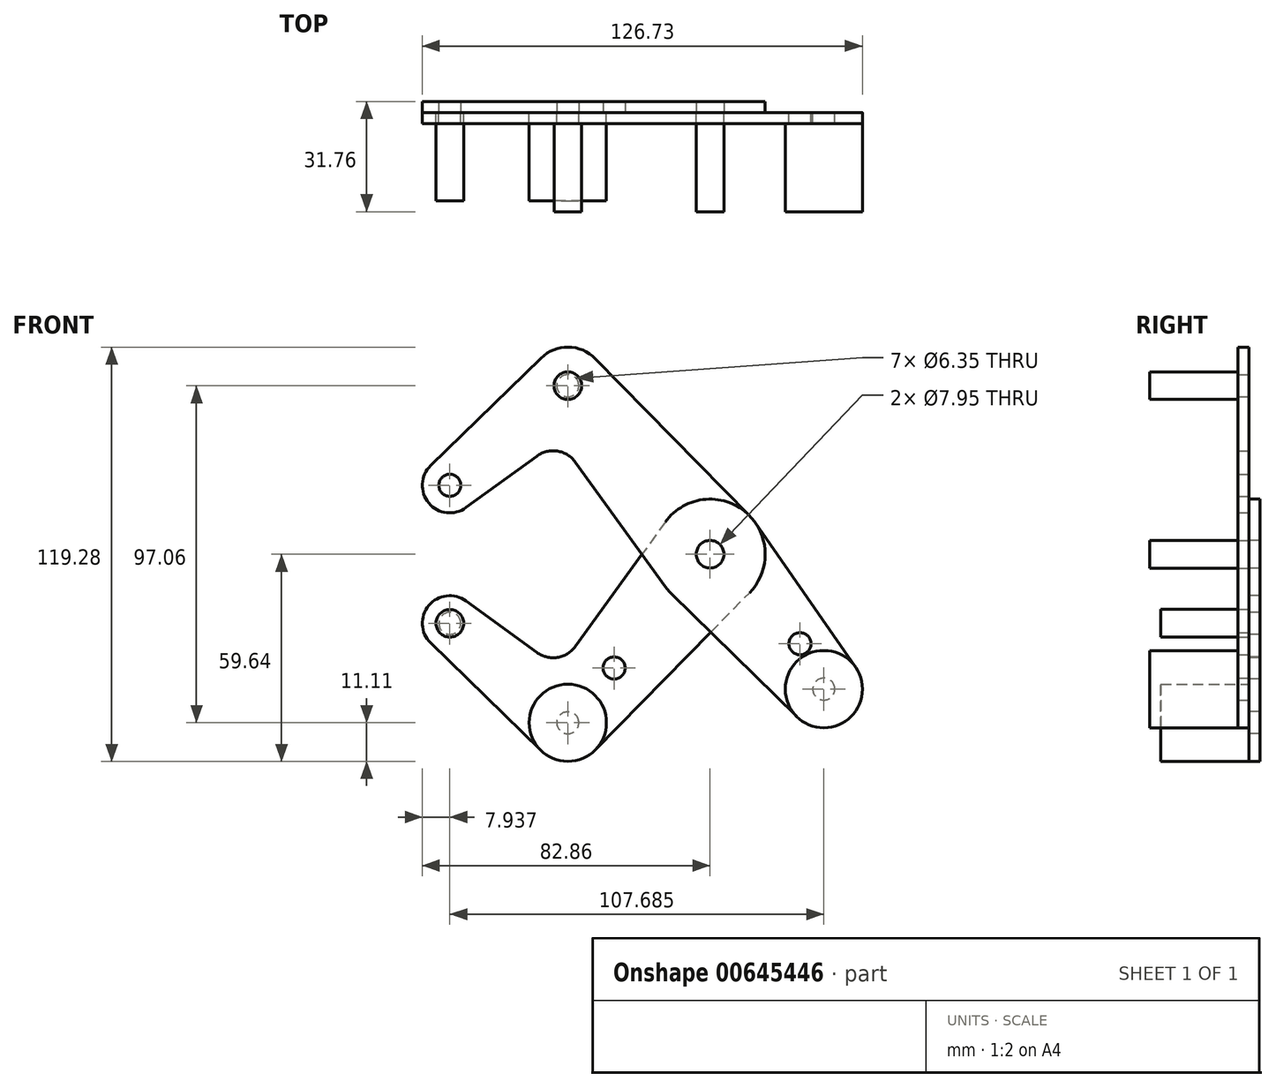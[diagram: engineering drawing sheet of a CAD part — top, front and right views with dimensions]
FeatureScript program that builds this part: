
annotation { "Feature Type Name" : "Feature", "Feature Type Description" : "" }
export const myFeature = defineFeature(function(context is Context, id is Id, definition is map)
    precondition{}
    {
        {
            var Q0;
            Q0=qCreatedBy(makeId("Front.planeOp"),FACE);
            var sketch = newSketch(context, id + "F0", { "sketchPlane" : qUnion([Q0])});
            skCircle(sketch, "E0", {"center": v(0, 0) * mm, "radius": 15.88 * mm});
            skCircle(sketch, "E1", {"center": v(0, 0) * mm, "radius": 3.98 * mm});
            skCircle(sketch, "E2", {"center": v(32.76, -38.82) * mm, "radius": 11.11 * mm});
            skLineSegment(sketch, "E3", {"start": v(-40.95, 48.53) * mm, "end": v(32.76, -38.82) * mm, "construction": true});
            skLineSegment(sketch, "E4", {"start": v(-40.95, 48.53) * mm, "end": v(-74.92, 19.86) * mm, "construction": true});
            skLineSegment(sketch, "E5", {"start": v(0, 0) * mm, "end": v(-40.95, -48.53) * mm, "construction": true});
            skCircle(sketch, "E6", {"center": v(32.76, -38.82) * mm, "radius": 3.18 * mm});
            skCircle(sketch, "E7", {"center": v(25.9, -25.76) * mm, "radius": 3.18 * mm});
            skCircle(sketch, "E8", {"center": v(-40.95, -48.53) * mm, "radius": 11.11 * mm});
            skCircle(sketch, "E9", {"center": v(-40.95, -48.53) * mm, "radius": 3.18 * mm});
            skCircle(sketch, "E10", {"center": v(-27.63, -32.75) * mm, "radius": 3.18 * mm});
            skLineSegment(sketch, "E11", {"start": v(-40.95, -48.53) * mm, "end": v(-74.92, -19.86) * mm, "construction": true});
            skCircle(sketch, "E12", {"center": v(-74.92, -19.86) * mm, "radius": 7.94 * mm});
            skCircle(sketch, "E13", {"center": v(-74.92, -19.86) * mm, "radius": 3.18 * mm});
            skCircle(sketch, "E14", {"center": v(-74.92, 19.86) * mm, "radius": 7.94 * mm});
            skCircle(sketch, "E15", {"center": v(-74.92, 19.86) * mm, "radius": 3.18 * mm});
            skCircle(sketch, "E16", {"center": v(-40.95, 48.53) * mm, "radius": 11.11 * mm});
            skCircle(sketch, "E17", {"center": v(-40.95, 48.53) * mm, "radius": 3.18 * mm});
            skLineSegment(sketch, "E18", {"start": v(-80.46, 25.55) * mm, "end": v(-48.7, 56.49) * mm});
            skLineSegment(sketch, "E19", {"start": v(-70.25, 13.45) * mm, "end": v(-49.88, 28.28) * mm});
            skLineSegment(sketch, "E20", {"start": v(-38.75, 26.52) * mm, "end": v(-12.87, -9.3) * mm});
            skArc(sketch, "E21.filletArc", {"start": v(-38.75, 26.52) * mm, "mid": v(-43.95, 29.7) * mm, "end": v(-49.88, 28.28) * mm});
            skLineSegment(sketch, "E22", {"start": v(-33.02, 56.31) * mm, "end": v(11.33, 11.12) * mm});
            skLineSegment(sketch, "E23", {"start": v(13.04, 9.06) * mm, "end": v(41.89, -32.48) * mm});
            skLineSegment(sketch, "E24", {"start": v(-11.12, -11.33) * mm, "end": v(24.98, -46.76) * mm});
            skLineSegment(sketch, "E25", {"start": v(-33.02, -56.31) * mm, "end": v(11.33, -11.12) * mm});
            skLineSegment(sketch, "E26", {"start": v(-80.46, -25.55) * mm, "end": v(-48.7, -56.49) * mm});
            skLineSegment(sketch, "E27", {"start": v(-12.87, 9.3) * mm, "end": v(-38.75, -26.52) * mm});
            skLineSegment(sketch, "E28", {"start": v(-70.25, -13.45) * mm, "end": v(-49.88, -28.28) * mm});
            skArc(sketch, "E29.filletArc", {"start": v(-49.88, -28.28) * mm, "mid": v(-43.95, -29.7) * mm, "end": v(-38.75, -26.52) * mm});
            skSolve(sketch);
        }
        {
            var Q0;
            Q0=makeQuery(id+"F0.imprint","IMPRINT",FACE,{"disambiguationData":[TD([[makeQuery(id+"F0.imprint","IMPRINT",EDGE,{"derivedFrom":sQuery(id+"F0.wireOp",EDGE,"E15")}),-1.0]])]});
            var Q1;
            {var subQ0=sQuery(id+"F0.wireOp",EDGE,"E18");Q1=makeQuery(id+"F0.imprint","IMPRINT",FACE,{"disambiguationData":[TD([[makeQuery(id+"F0.imprint","IMPRINT",EDGE,{"derivedFrom":subQ0}),-1.0]])]});}
            var Q2;
            Q2=makeQuery(id+"F0.imprint","IMPRINT",FACE,{"disambiguationData":[TD([[makeQuery(id+"F0.imprint","IMPRINT",EDGE,{"derivedFrom":sQuery(id+"F0.wireOp",EDGE,"E17")}),-1.0]])]});
            var Q3;
            Q3=makeQuery(id+"F0.imprint","IMPRINT",FACE,{"disambiguationData":[TD([[makeQuery(id+"F0.imprint","IMPRINT",EDGE,{"derivedFrom":sQuery(id+"F0.wireOp",EDGE,"E1")}),-1.0]])]});
            var Q4;
            Q4=makeQuery(id+"F0.imprint","IMPRINT",FACE,{"disambiguationData":[TD([[makeQuery(id+"F0.imprint","IMPRINT",EDGE,{"derivedFrom":sQuery(id+"F0.wireOp",EDGE,"E7")}),-1.0]])]});
            var Q5;
            Q5=makeQuery(id+"F0.imprint","IMPRINT",FACE,{"disambiguationData":[TD([[makeQuery(id+"F0.imprint","IMPRINT",EDGE,{"derivedFrom":sQuery(id+"F0.wireOp",EDGE,"E6")}),-1.0]])]});
            var Q6;
            {var subQ0=sQuery(id+"F0.wireOp",EDGE,"E20");var subQ1=sQuery(id+"F0.wireOp",EDGE,"E0");var subQ2=makeQuery(id+"F0.imprint","INTERSECT",VERTEX,{"derivedFrom":[subQ1,subQ0]});Q6=makeQuery(id+"F0.imprint","IMPRINT",FACE,{"disambiguationData":[TD([[makeQuery(id+"F0.imprint","IMPRINT",EDGE,{"disambiguationData":[TD([[subQ2,1.0]])],"derivedFrom":subQ1}),-1.0]])]});}
            var Q7;
            {var subQ0=sQuery(id+"F0.wireOp",EDGE,"E24");var subQ1=sQuery(id+"F0.wireOp",EDGE,"E0");var subQ2=makeQuery(id+"F0.imprint","INTERSECT",VERTEX,{"derivedFrom":[subQ1,subQ0]});Q7=makeQuery(id+"F0.imprint","IMPRINT",FACE,{"disambiguationData":[TD([[makeQuery(id+"F0.imprint","IMPRINT",EDGE,{"disambiguationData":[TD([[subQ2,-1.0]])],"derivedFrom":subQ1}),-1.0]])]});}
            extrude(context, id + "F1", {"entities" : qUnion([Q0, Q1, Q2, Q3, Q4, Q5, Q6, Q7]), "depth" : 3.17 * mm, "offsetDistance" : 25.4 * mm});
        }
        {
            var Q0;
            Q0=makeQuery(id+"F0.imprint","IMPRINT",FACE,{"disambiguationData":[TD([[makeQuery(id+"F0.imprint","IMPRINT",EDGE,{"derivedFrom":sQuery(id+"F0.wireOp",EDGE,"E13")}),-1.0]])]});
            var Q1;
            Q1=makeQuery(id+"F0.imprint","IMPRINT",FACE,{"disambiguationData":[TD([[makeQuery(id+"F0.imprint","IMPRINT",EDGE,{"derivedFrom":sQuery(id+"F0.wireOp",EDGE,"E10")}),-1.0]])]});
            var Q2;
            Q2=makeQuery(id+"F0.imprint","IMPRINT",FACE,{"disambiguationData":[TD([[makeQuery(id+"F0.imprint","IMPRINT",EDGE,{"derivedFrom":sQuery(id+"F0.wireOp",EDGE,"E1")}),-1.0]])]});
            var Q3;
            {var subQ0=sQuery(id+"F0.wireOp",EDGE,"E24");var subQ1=sQuery(id+"F0.wireOp",EDGE,"E0");var subQ2=makeQuery(id+"F0.imprint","INTERSECT",VERTEX,{"derivedFrom":[subQ1,subQ0]});Q3=makeQuery(id+"F0.imprint","IMPRINT",FACE,{"disambiguationData":[TD([[makeQuery(id+"F0.imprint","IMPRINT",EDGE,{"disambiguationData":[TD([[subQ2,-1.0]])],"derivedFrom":subQ1}),-1.0]])]});}
            var Q4;
            {var subQ0=sQuery(id+"F0.wireOp",EDGE,"E20");var subQ1=sQuery(id+"F0.wireOp",EDGE,"E0");var subQ2=makeQuery(id+"F0.imprint","INTERSECT",VERTEX,{"derivedFrom":[subQ1,subQ0]});Q4=makeQuery(id+"F0.imprint","IMPRINT",FACE,{"disambiguationData":[TD([[makeQuery(id+"F0.imprint","IMPRINT",EDGE,{"disambiguationData":[TD([[subQ2,1.0]])],"derivedFrom":subQ1}),-1.0]])]});}
            var Q5;
            Q5=makeQuery(id+"F0.imprint","IMPRINT",FACE,{"disambiguationData":[TD([[makeQuery(id+"F0.imprint","IMPRINT",EDGE,{"derivedFrom":sQuery(id+"F0.wireOp",EDGE,"E9")}),-1.0]])]});
            extrude(context, id + "F2", {"entities" : qUnion([Q0, Q1, Q2, Q3, Q4, Q5]), "oppositeDirection" : true, "depth" : 3.17 * mm, "offsetDistance" : 25.4 * mm});
        }
        {
            var Q0;
            Q0=makeQuery(id+"F1.opExtrude","CAP_FACE",FACE,{"disambiguationData":[OSD([sQuery(id+"F0.wireOp",EDGE,"E0"),sQuery(id+"F0.wireOp",EDGE,"E1"),sQuery(id+"F0.wireOp",EDGE,"E2"),sQuery(id+"F0.wireOp",EDGE,"E6"),sQuery(id+"F0.wireOp",EDGE,"E7"),sQuery(id+"F0.wireOp",EDGE,"E14"),sQuery(id+"F0.wireOp",EDGE,"E15"),sQuery(id+"F0.wireOp",EDGE,"E16"),sQuery(id+"F0.wireOp",EDGE,"E17"),sQuery(id+"F0.wireOp",EDGE,"E18"),sQuery(id+"F0.wireOp",EDGE,"E19"),sQuery(id+"F0.wireOp",EDGE,"E20"),sQuery(id+"F0.wireOp",EDGE,"E21.filletArc"),sQuery(id+"F0.wireOp",EDGE,"E22"),sQuery(id+"F0.wireOp",EDGE,"E23"),sQuery(id+"F0.wireOp",EDGE,"E24")])],"isStart":false});
            var sketch = newSketch(context, id + "F3", { "sketchPlane" : qUnion([Q0])});
            skCircle(sketch, "E30", {"center": v(0, 0) * mm, "radius": 3.98 * mm});
            skCircle(sketch, "E31", {"center": v(32.76, -38.82) * mm, "radius": 11.11 * mm});
            skCircle(sketch, "E32", {"center": v(-40.95, 48.53) * mm, "radius": 3.98 * mm});
            skSolve(sketch);
        }
        {
            var Q0;
            Q0=makeQuery(id+"F2.opExtrude","CAP_FACE",FACE,{"disambiguationData":[OSD([sQuery(id+"F0.wireOp",EDGE,"E0"),sQuery(id+"F0.wireOp",EDGE,"E1"),sQuery(id+"F0.wireOp",EDGE,"E8"),sQuery(id+"F0.wireOp",EDGE,"E9"),sQuery(id+"F0.wireOp",EDGE,"E10"),sQuery(id+"F0.wireOp",EDGE,"E12"),sQuery(id+"F0.wireOp",EDGE,"E13"),sQuery(id+"F0.wireOp",EDGE,"E25"),sQuery(id+"F0.wireOp",EDGE,"E26"),sQuery(id+"F0.wireOp",EDGE,"E27"),sQuery(id+"F0.wireOp",EDGE,"E28"),sQuery(id+"F0.wireOp",EDGE,"E29.filletArc")])],"isStart":true});
            var sketch = newSketch(context, id + "F4", { "sketchPlane" : qUnion([Q0])});
            skCircle(sketch, "E33", {"center": v(-40.95, -48.53) * mm, "radius": 11.11 * mm});
            skCircle(sketch, "E34", {"center": v(-74.92, -19.86) * mm, "radius": 3.98 * mm});
            skSolve(sketch);
        }
        {
            var Q0;
            Q0 = qSketchRegion(id + "F3", true);
            var Q1;
            Q1 = qSketchRegion(id + "F4", true);
            extrude(context, id + "F5", {"entities" : qUnion([Q0, Q1]), "depth" : 25.4 * mm, "offsetDistance" : 25.4 * mm});
        }
    });
